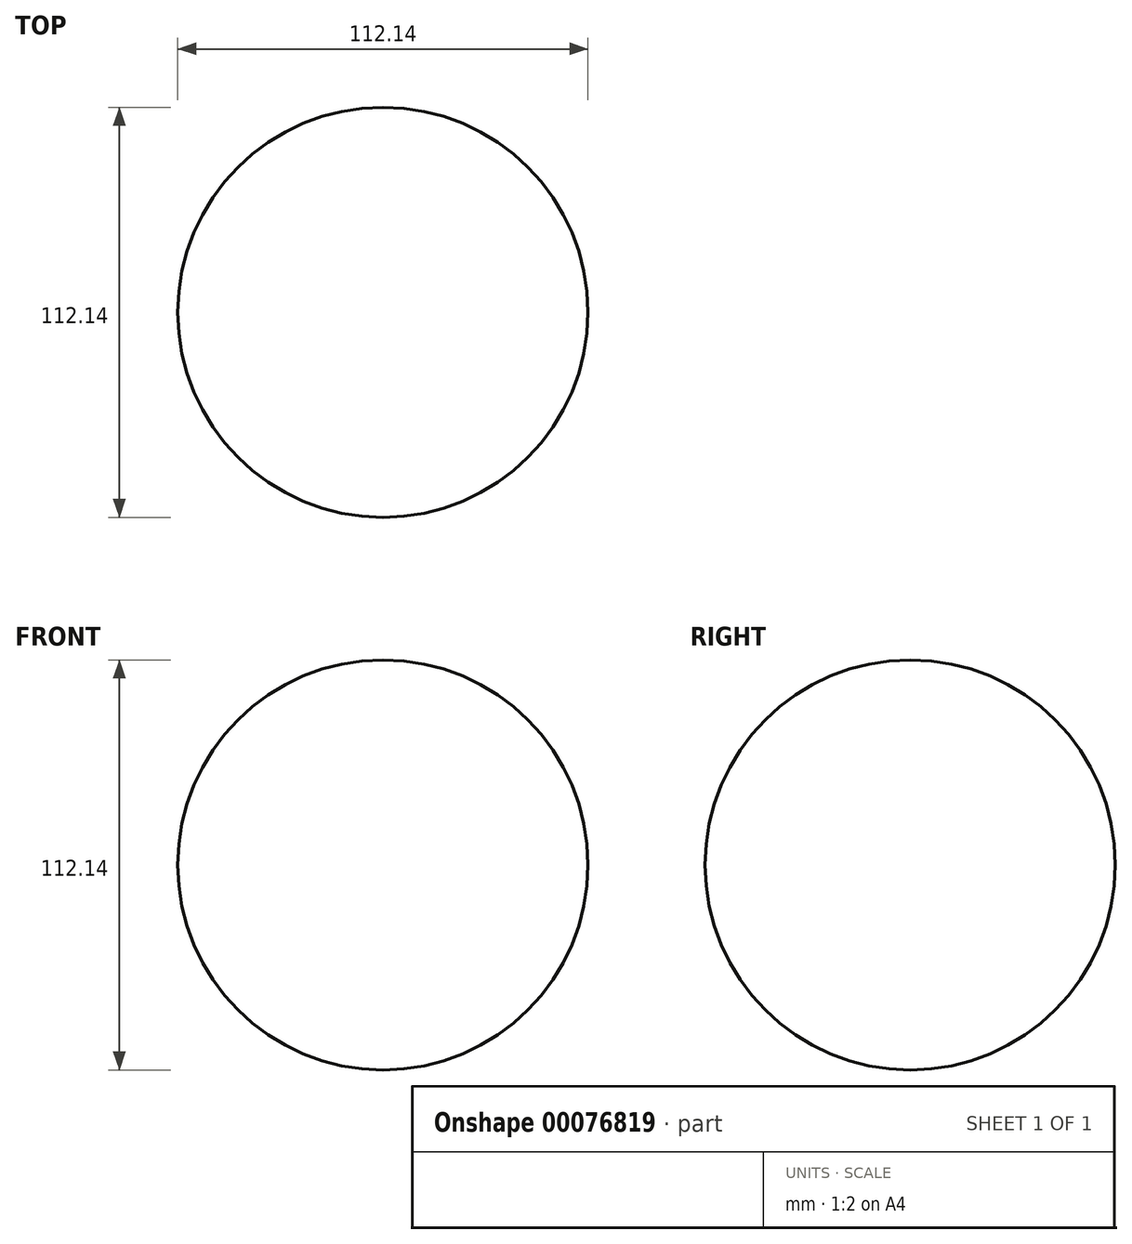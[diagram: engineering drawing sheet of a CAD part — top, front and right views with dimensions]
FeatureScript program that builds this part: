
annotation { "Feature Type Name" : "Feature", "Feature Type Description" : "" }
export const myFeature = defineFeature(function(context is Context, id is Id, definition is map)
    precondition{}
    {
        {
            var Q0;
            Q0=qCreatedBy(makeId("Front.planeOp"),FACE);
            var sketch = newSketch(context, id + "F0", { "sketchPlane" : qUnion([Q0])});
            skArc(sketch, "E0", {"start": v(0, -56.07) * mm, "mid": v(56.07, 0) * mm, "end": v(0, 56.07) * mm});
            skLineSegment(sketch, "E1", {"start": v(0, 56.07) * mm, "end": v(0, -56.07) * mm, "construction": true});
            skLineSegment(sketch, "E2", {"start": v(0, 56.07) * mm, "end": v(0, -56.07) * mm});
            skSolve(sketch);
        }
        {
            var Q0;
            Q0=makeQuery(id+"F0.imprint","IMPRINT",FACE,{"disambiguationData":[TD([[makeQuery(id+"F0.imprint","IMPRINT",EDGE,{"derivedFrom":sQuery(id+"F0.wireOp",EDGE,"E0")}),1.0]])]});
            var Q1;
            Q1=sQuery(id+"F0.wireOp",EDGE,"E2");
            revolve(context, id + "F1", {"entities" : qUnion([Q0]), "axis" : qUnion([Q1]), "revolveType" : RevolveType.FULL});
        }
    });
